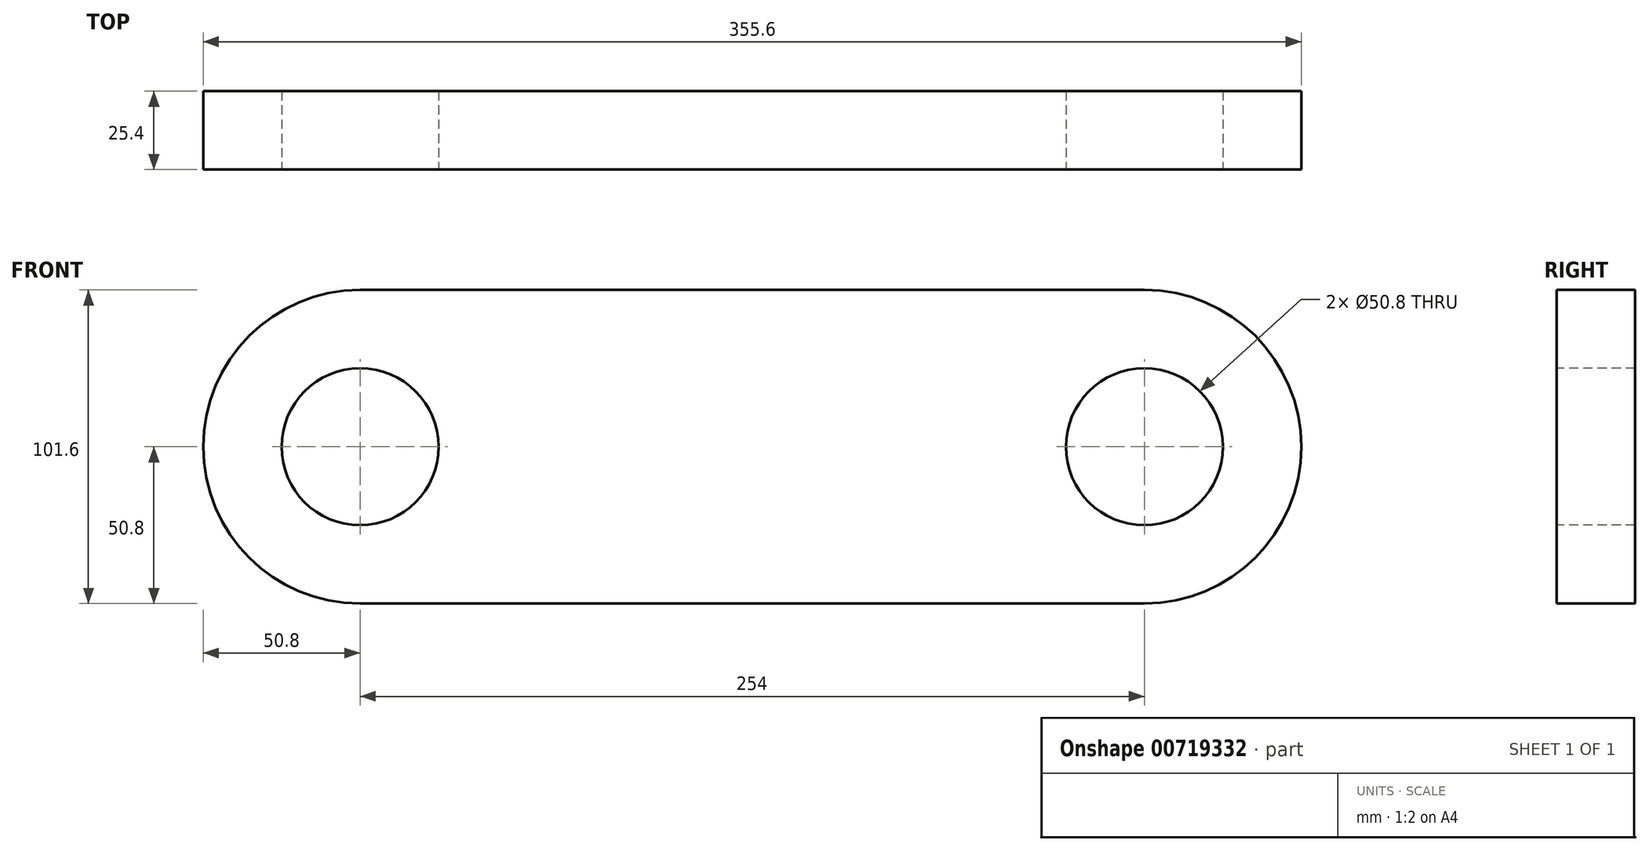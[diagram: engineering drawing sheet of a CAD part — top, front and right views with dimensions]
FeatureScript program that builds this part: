
annotation { "Feature Type Name" : "Feature", "Feature Type Description" : "" }
export const myFeature = defineFeature(function(context is Context, id is Id, definition is map)
    precondition{}
    {
        {
            var Q0;
            Q0=qCreatedBy(makeId("Front.planeOp"),FACE);
            var sketch = newSketch(context, id + "F0", { "sketchPlane" : qUnion([Q0])});
            skLineSegment(sketch, "E0.bottom", {"start": v(-127, 50.8) * mm, "end": v(127, 50.8) * mm});
            skLineSegment(sketch, "E0.top", {"start": v(-127, -50.8) * mm, "end": v(127, -50.8) * mm});
            skArc(sketch, "E1", {"start": v(-127, 50.8) * mm, "mid": v(-177.8, 0) * mm, "end": v(-127, -50.8) * mm});
            skArc(sketch, "E2", {"start": v(127, -50.8) * mm, "mid": v(177.8, 0) * mm, "end": v(127, 50.8) * mm});
            skSolve(sketch);
        }
        {
            var Q0;
            Q0 = qSketchRegion(id + "F0", true);
            extrude(context, id + "F1", {"entities" : qUnion([Q0]), "endBound" : BoundingType.SYMMETRIC, "depth" : 25.4 * mm, "offsetDistance" : 25.4 * mm});
        }
        {
            var Q0;
            Q0=makeQuery(id+"F1.opExtrude","CAP_FACE",FACE,{"disambiguationData":[OSD([sQuery(id+"F0.wireOp",EDGE,"E0.bottom"),sQuery(id+"F0.wireOp",EDGE,"E0.top"),sQuery(id+"F0.wireOp",EDGE,"E1"),sQuery(id+"F0.wireOp",EDGE,"E2")])],"isStart":false});
            var sketch = newSketch(context, id + "F2", { "sketchPlane" : qUnion([Q0])});
            skCircle(sketch, "E3", {"center": v(-127, 0) * mm, "radius": 25.4 * mm});
            skCircle(sketch, "E4", {"center": v(127, 0) * mm, "radius": 25.4 * mm});
            skSolve(sketch);
        }
        {
            var Q0;
            Q0 = qSketchRegion(id + "F2", true);
            extrude(context, id + "F3", {"entities" : qUnion([Q0]), "operationType" : NewBodyOperationType.REMOVE, "endBound" : BoundingType.THROUGH_ALL, "oppositeDirection" : true, "depth" : 25.4 * mm, "offsetDistance" : 25.4 * mm});
        }
    });
